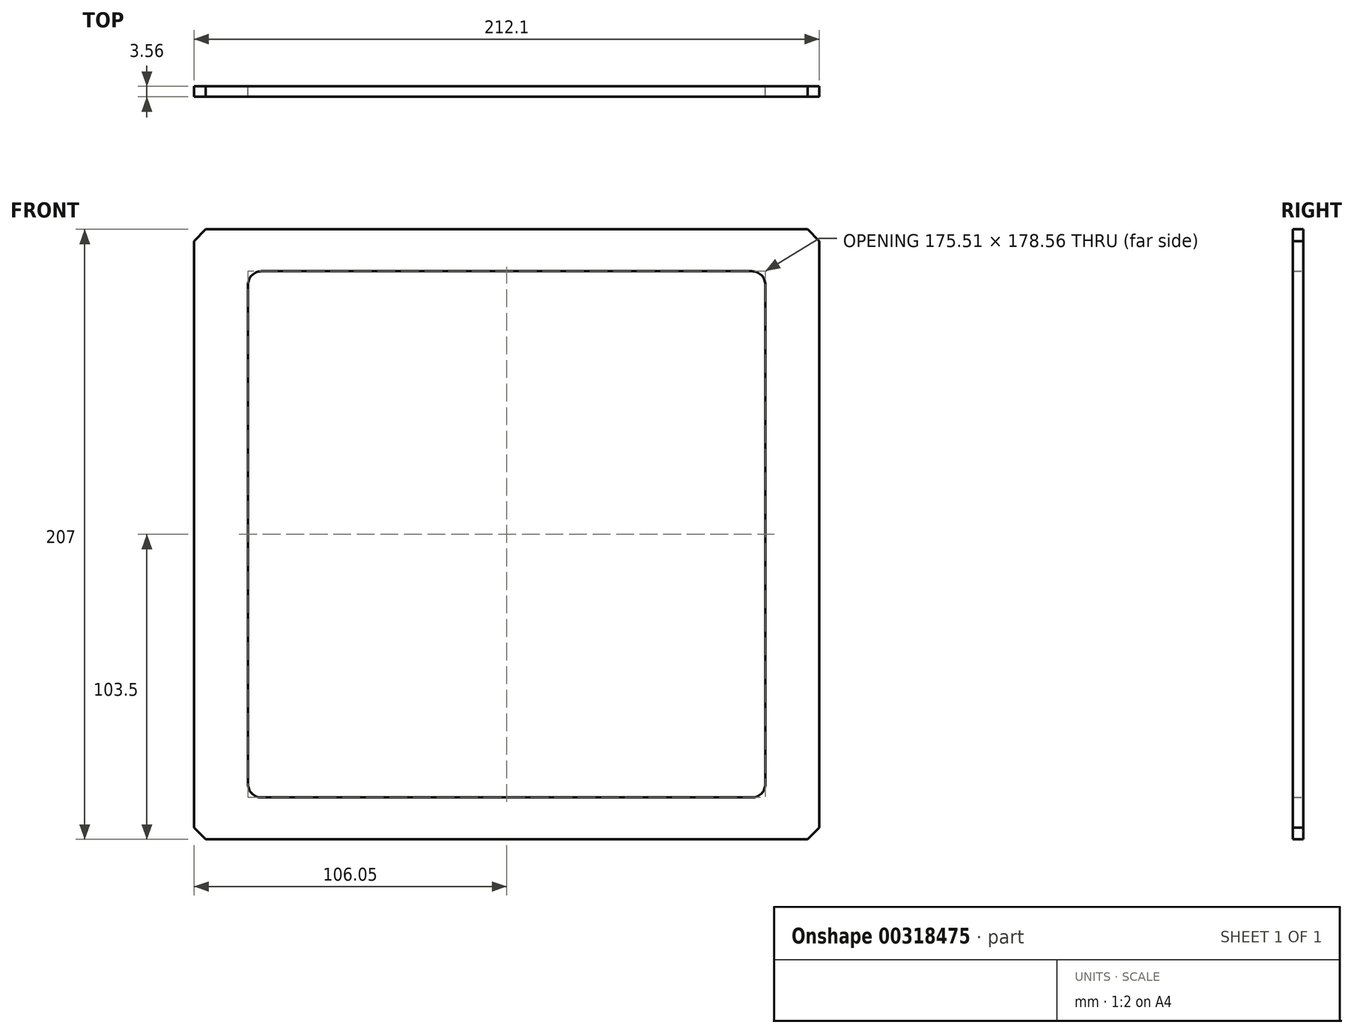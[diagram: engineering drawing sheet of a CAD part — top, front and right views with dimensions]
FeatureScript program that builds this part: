
annotation { "Feature Type Name" : "Feature", "Feature Type Description" : "" }
export const myFeature = defineFeature(function(context is Context, id is Id, definition is map)
    precondition{}
    {
        {
            var Q0;
            Q0=qCreatedBy(makeId("Front.planeOp"),FACE);
            var sketch = newSketch(context, id + "F0", { "sketchPlane" : qUnion([Q0])});
            skLineSegment(sketch, "E0.bottom", {"start": v(-106.05, -103.5) * mm, "end": v(106.05, -103.5) * mm});
            skLineSegment(sketch, "E0.top", {"start": v(-106.05, 103.5) * mm, "end": v(106.04, 103.5) * mm});
            skLineSegment(sketch, "E0.left", {"start": v(-106.05, -103.5) * mm, "end": v(-106.05, 103.5) * mm});
            skLineSegment(sketch, "E0.right", {"start": v(106.05, -103.5) * mm, "end": v(106.04, 103.5) * mm});
            skPoint(sketch, "E0.middle", {"position": v(0, 0) * mm});
            skLineSegment(sketch, "E1.bottom", {"start": v(-83.18, -89.28) * mm, "end": v(83.18, -89.28) * mm});
            skLineSegment(sketch, "E1.top", {"start": v(-83.18, 89.28) * mm, "end": v(83.18, 89.28) * mm});
            skLineSegment(sketch, "E1.left", {"start": v(-87.76, -84.7) * mm, "end": v(-87.76, 84.7) * mm});
            skLineSegment(sketch, "E1.right", {"start": v(87.76, -84.7) * mm, "end": v(87.76, 84.7) * mm});
            skPoint(sketch, "E2.visualSharp", {"position": v(-87.76, 89.28) * mm});
            skArc(sketch, "E2.filletArc", {"start": v(-83.18, 89.28) * mm, "mid": v(-86.42, 87.94) * mm, "end": v(-87.76, 84.7) * mm});
            skPoint(sketch, "E3.visualSharp", {"position": v(87.76, 89.28) * mm});
            skArc(sketch, "E3.filletArc", {"start": v(87.76, 84.7) * mm, "mid": v(86.42, 87.94) * mm, "end": v(83.18, 89.28) * mm});
            skPoint(sketch, "E4.visualSharp", {"position": v(87.76, -89.28) * mm});
            skArc(sketch, "E4.filletArc", {"start": v(83.18, -89.28) * mm, "mid": v(86.42, -87.94) * mm, "end": v(87.76, -84.7) * mm});
            skPoint(sketch, "E5.visualSharp", {"position": v(-87.76, -89.28) * mm});
            skArc(sketch, "E5.filletArc", {"start": v(-87.76, -84.7) * mm, "mid": v(-86.42, -87.94) * mm, "end": v(-83.18, -89.28) * mm});
            skLineSegment(sketch, "E6", {"start": v(-102.1, 103.5) * mm, "end": v(-106.05, 99.55) * mm});
            skLineSegment(sketch, "E7", {"start": v(102.1, 103.5) * mm, "end": v(106.05, 99.55) * mm});
            skLineSegment(sketch, "E8", {"start": v(-106.05, -99.55) * mm, "end": v(-102.1, -103.5) * mm});
            skLineSegment(sketch, "E9", {"start": v(106.05, -99.55) * mm, "end": v(102.1, -103.5) * mm});
            skSolve(sketch);
        }
        {
            var Q0;
            Q0=makeQuery(id+"F0.imprint","IMPRINT",FACE,{"disambiguationData":[TD([[makeQuery(id+"F0.imprint","IMPRINT",EDGE,{"derivedFrom":sQuery(id+"F0.wireOp",EDGE,"E1.bottom")}),-1.0]])]});
            extrude(context, id + "F1", {"entities" : qUnion([Q0]), "offsetDistance" : 25.4 * mm, "depth" : 3.56 * mm});
        }
    });
